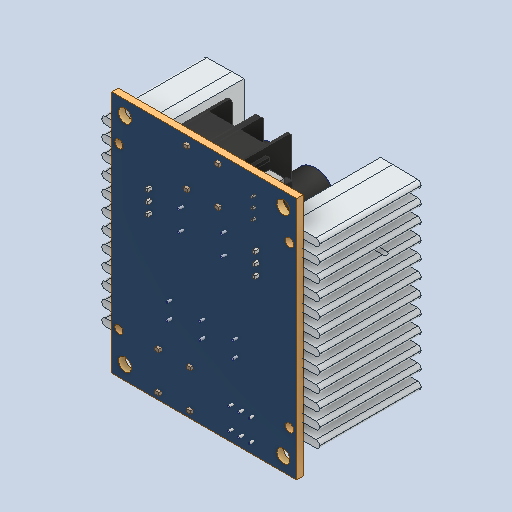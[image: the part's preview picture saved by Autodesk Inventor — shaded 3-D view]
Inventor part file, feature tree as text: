
AUTODESK INVENTOR PART (.ipt)
format: ipt  version: 2023 (Build 270158000, 158)  size: 6,534,144 bytes
history: native  units: mm
features: other x38, helix x37, surface_op x2
ambient origin geometry x8: Origin, YZ Plane, XZ Plane, XY Plane, X Axis, Y Axis, Z Axis, Center Point
bodies: Solid1 (feature_tree), Solid2 (feature_tree), Solid3 (feature_tree), Solid4 (feature_tree), Solid5 (feature_tree), Solid6 (feature_tree), Solid7 (feature_tree), Solid8 (feature_tree), Solid9 (feature_tree), Solid10 (feature_tree), Solid11 (feature_tree), Solid12 (feature_tree), Solid13 (feature_tree), Solid14 (feature_tree), Solid15 (feature_tree), Solid16 (feature_tree), Solid17 (feature_tree), Solid18 (feature_tree), Solid19 (feature_tree), Solid20 (feature_tree), Solid21 (feature_tree), Solid22 (feature_tree), Solid23 (feature_tree), Solid24 (feature_tree), Solid25 (feature_tree), Solid26 (feature_tree), Solid27 (feature_tree), Solid28 (feature_tree), Solid29 (feature_tree), Solid30 (feature_tree), Solid31 (feature_tree), Solid32 (feature_tree), Solid33 (feature_tree), Solid34 (feature_tree), Solid35 (feature_tree), Solid36 (feature_tree), Solid37 (feature_tree), Solid38 (feature_tree), Solid39 (feature_tree), Solid40 (feature_tree), Solid41 (feature_tree), Solid42 (feature_tree), Solid43 (feature_tree), Solid44 (feature_tree), Solid45 (feature_tree), Solid46 (feature_tree), Solid47 (feature_tree), Solid48 (feature_tree), Solid49 (feature_tree), Solid50 (feature_tree), Solid51 (feature_tree), Solid52 (feature_tree), Solid53 (feature_tree), Solid54 (feature_tree), Solid55 (feature_tree), Solid56 (feature_tree), Solid57 (feature_tree), Solid58 (feature_tree), Solid59 (feature_tree), Solid60 (feature_tree), Solid61 (feature_tree), Solid62 (feature_tree), Solid63 (feature_tree), Solid64 (feature_tree), Solid65 (feature_tree), Solid66 (feature_tree), Solid67 (feature_tree), Solid68 (feature_tree), Solid69 (feature_tree), Solid70 (feature_tree), Solid71 (feature_tree), Solid72 (feature_tree), Solid73 (feature_tree), Solid74 (feature_tree), Solid75 (feature_tree), Solid76 (feature_tree), Solid77 (feature_tree)
feature tree (77):
  other  "heatsink 45x10x12r_1:1"
  other  "pcb_2:1"
  other  "heatsink 45x10x12r_3:1"
  helix  "coil_4:1"  [1 undecoded]
  helix  "coil_4:2"  [1 undecoded]
  helix  "coil_4:3"  [1 undecoded]
  helix  "coil_4:4"  [1 undecoded]
  helix  "coil_4:5"  [1 undecoded]
  helix  "coil_4:6"  [1 undecoded]
  helix  "coil_4:7"  [1 undecoded]
  helix  "coil_4:8"  [1 undecoded]
  helix  "coil_4:9"  [1 undecoded]
  helix  "coil_4:10"  [1 undecoded]
  helix  "coil_4:11"  [1 undecoded]
  helix  "coil_4:12"  [1 undecoded]
  helix  "coil_4:13"  [1 undecoded]
  helix  "coil_4:14"  [1 undecoded]
  helix  "coil_4:15"  [1 undecoded]
  helix  "coil_4:16"  [1 undecoded]
  helix  "coil_4:17"  [1 undecoded]
  helix  "coil_4:18"  [1 undecoded]
  helix  "coil_4:19"  [1 undecoded]
  helix  "coil_4:20"  [1 undecoded]
  helix  "coil_4:21"  [1 undecoded]
  helix  "coil_4:22"  [1 undecoded]
  helix  "coil_4:23"  [1 undecoded]
  helix  "coil_4:24"  [1 undecoded]
  helix  "coil_4:25"  [1 undecoded]
  helix  "coil_4:26"  [1 undecoded]
  helix  "coil_4:27"  [1 undecoded]
  helix  "coil_4:28"  [1 undecoded]
  helix  "coil_4:29"  [1 undecoded]
  helix  "coil_4:30"  [1 undecoded]
  helix  "coil_4:31"  [1 undecoded]
  helix  "coil_4:32"  [1 undecoded]
  helix  "coil_4:33"  [1 undecoded]
  helix  "coil_4:34"  [1 undecoded]
  helix  "coil_4:35"  [1 undecoded]
  helix  "coil_4:36"  [1 undecoded]
  helix  "coil_4:37"  [1 undecoded]
  other  "terminal-Base_18:1"
  other  "screw pad_19:1"
  other  "screw-term_20:1"
  other  "screw pad_21:1"
  other  "screw-term_22:1"
  other  "terminal-Base_18:2"
  other  "screw pad_19:2"
  other  "screw-term_20:2"
  other  "screw pad_21:2"
  other  "screw-term_22:2"
  surface_op  "Trimpot 3296W_Valor predeterminado_7:1"
  surface_op  "Trimpot 3296W_Valor predeterminado_8:1"
  other  "c20x10x5_9:1"
  other  "c20x10x5_9:2"
  other  "c20x10x5_10:1"
  other  "c20x10x5_10:2"
  other  "c20x8x4_11:1"
  other  "c20x8x4_11:2"
  other  "c20x8x4_12:1"
  other  "c20x8x4_12:2"
  other  "c20x8x4_13:1"
  other  "c20x8x4_13:2"
  other  "MOSFET_14:1"
  other  "MOSFET_14:2"
  other  "MOSFET_14:3"
  other  "MOSFET_14:4"
  other  "MOSFET_14:5"
  other  "MOSFET_15:1"
  other  "MOSFET_15:2"
  other  "MOSFET_15:3"
  other  "MOSFET_15:4"
  other  "MOSFET_15:5"
  other  "3mm LED_16:1"
  other  "3mm LED_16:2"
  other  "3mm LED_16:3"
  other  "3mm LED_16:4"
  other  "Selector Switch - SS12D00_17:1"
note: 37 required parameter values undecoded (feature->parameter linkage not recoverable at this tier; creation-order binding heuristic only, values carry confidence <= 0.55)
